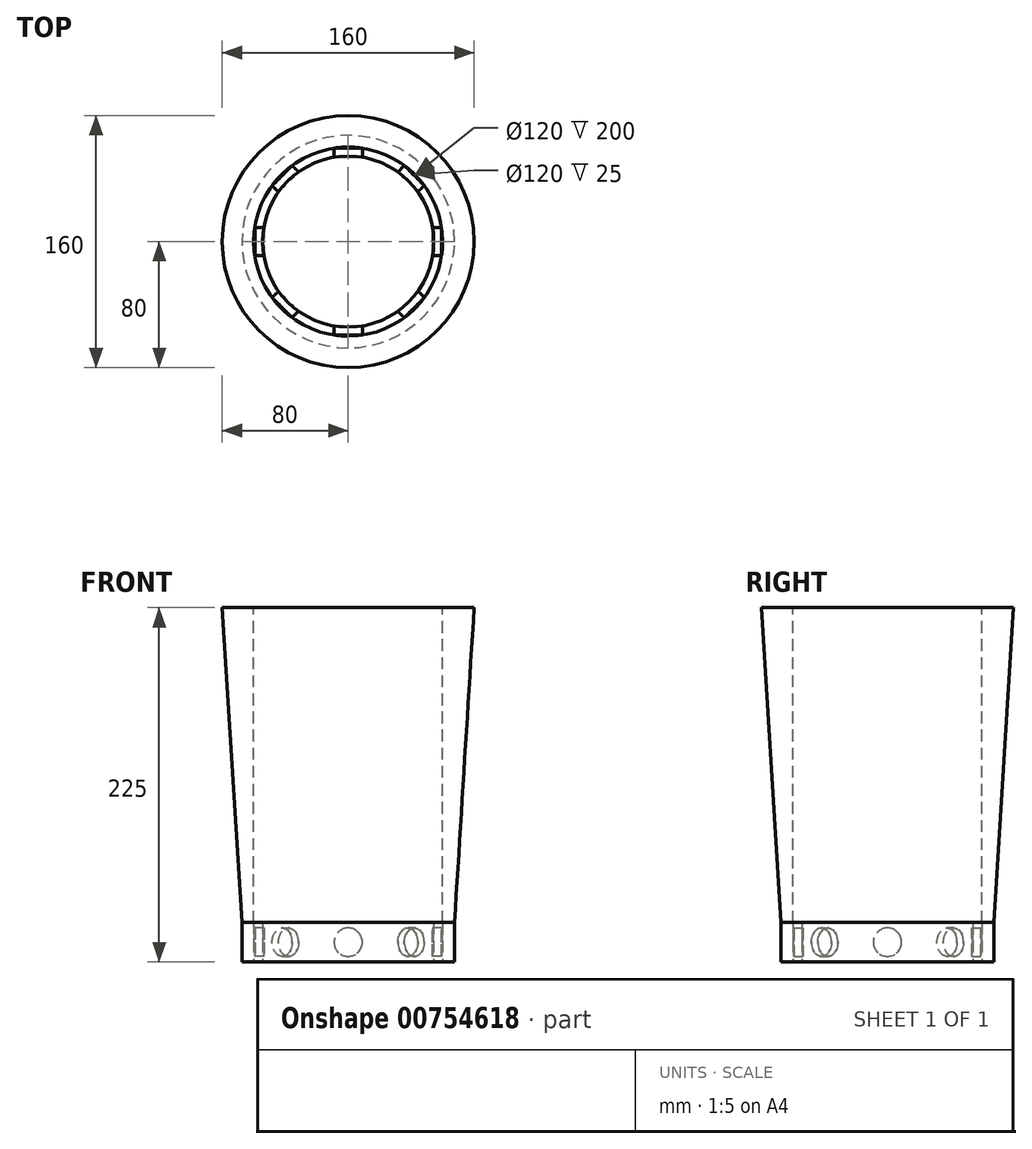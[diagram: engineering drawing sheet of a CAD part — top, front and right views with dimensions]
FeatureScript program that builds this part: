
annotation { "Feature Type Name" : "Feature", "Feature Type Description" : "" }
export const myFeature = defineFeature(function(context is Context, id is Id, definition is map)
    precondition{}
    {
        {
            var Q0;
            Q0=qCreatedBy(makeId("Top.planeOp"),FACE);
            var sketch = newSketch(context, id + "F0", { "sketchPlane" : qUnion([Q0])});
            skCircle(sketch, "E0", {"center": v(0, 0) * mm, "radius": 67.5 * mm});
            skSolve(sketch);
        }
        {
            var Q0;
            Q0=qCreatedBy(makeId("Top.planeOp"),FACE);
            cPlane(context, id + "F1", {"entities" : qUnion([Q0]), "cplaneType" : CPlaneType.OFFSET, "offset" : 200 * mm, "width" : 150 * mm, "height" : 150 * mm});
        }
        {
            var Q0;
            Q0=qCreatedBy(id+"F1.planeOp",FACE);
            var sketch = newSketch(context, id + "F2", { "sketchPlane" : qUnion([Q0])});
            skPoint(sketch, "E1", {"position": v(0, 0) * mm});
            skCircle(sketch, "E2", {"center": v(0, 0) * mm, "radius": 80 * mm});
            skSolve(sketch);
        }
        {
            var Q0;
            Q0=makeQuery(id+"F0.imprint","IMPRINT",FACE,{"disambiguationData":[TD([[makeQuery(id+"F0.imprint","IMPRINT",EDGE,{"derivedFrom":sQuery(id+"F0.wireOp",EDGE,"E0")}),1.0]])]});
            var Q1;
            Q1=makeQuery(id+"F2.imprint","IMPRINT",FACE,{"disambiguationData":[TD([[makeQuery(id+"F2.imprint","IMPRINT",EDGE,{"derivedFrom":sQuery(id+"F2.wireOp",EDGE,"E2")}),1.0]])]});
            loft(context, id + "F3", {"sheetProfilesArray" : [{ "sheetProfileEntities" : qUnion([Q0]) }, { "sheetProfileEntities" : qUnion([Q1]) }]});
        }
        {
            var Q0;
            Q0=makeQuery(id+"F3.opLoft","CAP_FACE",FACE,{"disambiguationData":[OSD([makeQuery(id+"F2.imprint","IMPRINT",FACE,{"disambiguationData":[TD([[makeQuery(id+"F2.imprint","IMPRINT",EDGE,{"derivedFrom":sQuery(id+"F2.wireOp",EDGE,"E2")}),1.0]])]})])],"isStart":true});
            var sketch = newSketch(context, id + "F4", { "sketchPlane" : qUnion([Q0])});
            skCircle(sketch, "E3", {"center": v(0, 0) * mm, "radius": 60 * mm});
            skSolve(sketch);
        }
        {
            var Q0;
            Q0=makeQuery(id+"F4.imprint","IMPRINT",FACE,{"disambiguationData":[TD([[makeQuery(id+"F4.imprint","IMPRINT",EDGE,{"derivedFrom":sQuery(id+"F4.wireOp",EDGE,"E3")}),1.0]])]});
            extrude(context, id + "F5", {"entities" : qUnion([Q0]), "operationType" : NewBodyOperationType.REMOVE, "oppositeDirection" : true, "depth" : 200 * mm, "offsetDistance" : 25 * mm});
        }
        {
            var Q0;
            Q0=qCreatedBy(makeId("Top.planeOp"),FACE);
            cPlane(context, id + "F6", {"entities" : qUnion([Q0]), "cplaneType" : CPlaneType.OFFSET, "offset" : 12.5 * mm, "oppositeDirection" : true, "width" : 150 * mm, "height" : 150 * mm});
        }
        {
            var Q0;
            Q0=qCreatedBy(id+"F6.planeOp",FACE);
            var sketch = newSketch(context, id + "F7", { "sketchPlane" : qUnion([Q0])});
            skPoint(sketch, "E4", {"position": v(0, 0) * mm});
            skCircle(sketch, "E5", {"center": v(0, 0) * mm, "radius": 67.5 * mm});
            skCircle(sketch, "E6", {"center": v(0, 0) * mm, "radius": 60 * mm});
            skLineSegment(sketch, "E7", {"start": v(-93.29, 0) * mm, "end": v(108.22, 0) * mm});
            skLineSegment(sketch, "E8", {"start": v(0, 89.91) * mm, "end": v(0, -108.53) * mm});
            skLineSegment(sketch, "E9", {"start": v(0, 0) * mm, "end": v(91.24, 91.24) * mm});
            skPoint(sketch, "E10", {"position": v(60, 0) * mm});
            skPoint(sketch, "E11", {"position": v(54.32, 0) * mm});
            skLineSegment(sketch, "E12", {"start": v(0, 0) * mm, "end": v(78.64, -78.64) * mm});
            skLineSegment(sketch, "E13", {"start": v(0, 0) * mm, "end": v(-76.82, -76.82) * mm});
            skLineSegment(sketch, "E14", {"start": v(0, 0) * mm, "end": v(-81.4, 81.4) * mm});
            skPoint(sketch, "E15", {"position": v(38.41, -38.41) * mm});
            skPoint(sketch, "E16", {"position": v(42.43, -42.43) * mm});
            skPoint(sketch, "E17", {"position": v(0, -60) * mm});
            skPoint(sketch, "E18", {"position": v(0, -54.32) * mm});
            skPoint(sketch, "E19", {"position": v(-42.43, -42.43) * mm});
            skPoint(sketch, "E20", {"position": v(-38.41, -38.41) * mm});
            skPoint(sketch, "E21", {"position": v(-60, 0) * mm});
            skPoint(sketch, "E22", {"position": v(-54.32, 0) * mm});
            skPoint(sketch, "E23", {"position": v(-42.43, 42.43) * mm});
            skPoint(sketch, "E24", {"position": v(-38.41, 38.41) * mm});
            skPoint(sketch, "E25", {"position": v(0, 60) * mm});
            skPoint(sketch, "E26", {"position": v(0, 54.32) * mm});
            skCircle(sketch, "E27", {"center": v(0, 0) * mm, "radius": 54.32 * mm});
            skPoint(sketch, "E28", {"position": v(-9, -59.32) * mm});
            skLineSegment(sketch, "E29", {"start": v(-9, -59.32) * mm, "end": v(-9, -53.57) * mm});
            skPoint(sketch, "E30", {"position": v(35.58, -48.31) * mm});
            skLineSegment(sketch, "E31", {"start": v(35.58, -48.31) * mm, "end": v(31.52, -44.24) * mm});
            skPoint(sketch, "E32", {"position": v(59.32, -9) * mm});
            skLineSegment(sketch, "E33", {"start": v(59.32, -9) * mm, "end": v(53.57, -9) * mm});
            skPoint(sketch, "E34", {"position": v(48.31, 35.58) * mm});
            skLineSegment(sketch, "E35", {"start": v(48.31, 35.58) * mm, "end": v(44.24, 31.52) * mm});
            skPoint(sketch, "E36", {"position": v(9, 59.32) * mm});
            skLineSegment(sketch, "E37", {"start": v(9, 59.32) * mm, "end": v(9, 53.57) * mm});
            skPoint(sketch, "E38", {"position": v(-35.58, 48.31) * mm});
            skLineSegment(sketch, "E39", {"start": v(-35.58, 48.31) * mm, "end": v(-31.52, 44.24) * mm});
            skPoint(sketch, "E40", {"position": v(-59.32, 9) * mm});
            skLineSegment(sketch, "E41", {"start": v(-59.32, 9) * mm, "end": v(-53.57, 9) * mm});
            skPoint(sketch, "E42", {"position": v(-48.31, -35.58) * mm});
            skLineSegment(sketch, "E43", {"start": v(-48.31, -35.58) * mm, "end": v(-44.24, -31.52) * mm});
            skSolve(sketch);
        }
        {
            var Q0;
            {var subQ0=sQuery(id+"F7.wireOp",EDGE,"E35");Q0=makeQuery(id+"F7.imprint","IMPRINT",FACE,{"disambiguationData":[TD([[makeQuery(id+"F7.imprint","IMPRINT",EDGE,{"derivedFrom":subQ0}),-1.0]])]});}
            var Q1;
            Q1=sQuery(id+"F7.wireOp",EDGE,"E9");
            revolve(context, id + "F8", {"operationType" : NewBodyOperationType.ADD, "surfaceOperationType" : NewSurfaceOperationType.NEW, "entities" : qUnion([Q0]), "axis" : qUnion([Q1]), "revolveType" : RevolveType.FULL});
        }
        {
            var Q0;
            {var subQ0=sQuery(id+"F7.wireOp",EDGE,"E29");Q0=makeQuery(id+"F7.imprint","IMPRINT",FACE,{"disambiguationData":[TD([[makeQuery(id+"F7.imprint","IMPRINT",EDGE,{"derivedFrom":subQ0}),-1.0]])]});}
            var Q1;
            {var subQ0=sQuery(id+"F7.wireOp",EDGE,"E37");Q1=makeQuery(id+"F7.imprint","IMPRINT",FACE,{"disambiguationData":[TD([[makeQuery(id+"F7.imprint","IMPRINT",EDGE,{"derivedFrom":subQ0}),-1.0]])]});}
            var Q2;
            Q2=sQuery(id+"F7.wireOp",EDGE,"E8");
            revolve(context, id + "F9", {"operationType" : NewBodyOperationType.ADD, "surfaceOperationType" : NewSurfaceOperationType.NEW, "entities" : qUnion([Q0, Q1]), "axis" : qUnion([Q2]), "revolveType" : RevolveType.FULL});
        }
        {
            var Q0;
            {var subQ0=sQuery(id+"F7.wireOp",EDGE,"E31");Q0=makeQuery(id+"F7.imprint","IMPRINT",FACE,{"disambiguationData":[TD([[makeQuery(id+"F7.imprint","IMPRINT",EDGE,{"derivedFrom":subQ0}),-1.0]])]});}
            var Q1;
            Q1=sQuery(id+"F7.wireOp",EDGE,"E12");
            revolve(context, id + "F10", {"operationType" : NewBodyOperationType.ADD, "surfaceOperationType" : NewSurfaceOperationType.NEW, "entities" : qUnion([Q0]), "axis" : qUnion([Q1]), "revolveType" : RevolveType.FULL});
        }
        {
            var Q0;
            {var subQ0=sQuery(id+"F7.wireOp",EDGE,"E39");Q0=makeQuery(id+"F7.imprint","IMPRINT",FACE,{"disambiguationData":[TD([[makeQuery(id+"F7.imprint","IMPRINT",EDGE,{"derivedFrom":subQ0}),-1.0]])]});}
            var Q1;
            Q1=sQuery(id+"F7.wireOp",EDGE,"E14");
            revolve(context, id + "F11", {"operationType" : NewBodyOperationType.ADD, "surfaceOperationType" : NewSurfaceOperationType.NEW, "entities" : qUnion([Q0]), "axis" : qUnion([Q1]), "revolveType" : RevolveType.FULL});
        }
        {
            var Q0;
            {var subQ0=sQuery(id+"F7.wireOp",EDGE,"E33");Q0=makeQuery(id+"F7.imprint","IMPRINT",FACE,{"disambiguationData":[TD([[makeQuery(id+"F7.imprint","IMPRINT",EDGE,{"derivedFrom":subQ0}),-1.0]])]});}
            var Q1;
            {var subQ0=sQuery(id+"F7.wireOp",EDGE,"E41");Q1=makeQuery(id+"F7.imprint","IMPRINT",FACE,{"disambiguationData":[TD([[makeQuery(id+"F7.imprint","IMPRINT",EDGE,{"derivedFrom":subQ0}),-1.0]])]});}
            var Q2;
            Q2=sQuery(id+"F7.wireOp",EDGE,"E7");
            revolve(context, id + "F12", {"operationType" : NewBodyOperationType.ADD, "surfaceOperationType" : NewSurfaceOperationType.NEW, "entities" : qUnion([Q0, Q1]), "axis" : qUnion([Q2]), "revolveType" : RevolveType.FULL});
        }
        {
            var Q0;
            {var subQ0=sQuery(id+"F7.wireOp",EDGE,"E43");Q0=makeQuery(id+"F7.imprint","IMPRINT",FACE,{"disambiguationData":[TD([[makeQuery(id+"F7.imprint","IMPRINT",EDGE,{"derivedFrom":subQ0}),-1.0]])]});}
            var Q1;
            Q1=sQuery(id+"F7.wireOp",EDGE,"E13");
            revolve(context, id + "F13", {"operationType" : NewBodyOperationType.ADD, "surfaceOperationType" : NewSurfaceOperationType.NEW, "entities" : qUnion([Q0]), "axis" : qUnion([Q1]), "revolveType" : RevolveType.FULL});
        }
        {
            var Q0;
            {var subQ0=sQuery(id+"F7.wireOp",EDGE,"E8");var subQ1=sQuery(id+"F7.wireOp",EDGE,"E5");var subQ2=makeQuery(id+"F7.imprint","INTERSECT",VERTEX,{"disambiguationData":[OD(1.0)],"derivedFrom":[subQ1,subQ0]});Q0=makeQuery(id+"F7.imprint","IMPRINT",FACE,{"disambiguationData":[TD([[makeQuery(id+"F7.imprint","IMPRINT",EDGE,{"disambiguationData":[TD([[subQ2,-1.0]])],"derivedFrom":subQ1}),1.0]])]});}
            var Q1;
            {var subQ4=sQuery(id+"F7.wireOp",EDGE,"E13");var subQ6=sQuery(id+"F7.wireOp",EDGE,"E5");var subQ8=makeQuery(id+"F7.imprint","INTERSECT",VERTEX,{"derivedFrom":[subQ6,subQ4]});Q1=makeQuery(id+"F7.imprint","IMPRINT",FACE,{"disambiguationData":[TD([[makeQuery(id+"F7.imprint","IMPRINT",EDGE,{"disambiguationData":[TD([[subQ8,-1.0]])],"derivedFrom":subQ6}),1.0]])]});}
            var Q2;
            {var subQ4=sQuery(id+"F7.wireOp",EDGE,"E7");var subQ6=sQuery(id+"F7.wireOp",EDGE,"E5");var subQ7=makeQuery(id+"F7.imprint","INTERSECT",VERTEX,{"disambiguationData":[OD(1.0)],"derivedFrom":[subQ6,subQ4]});Q2=makeQuery(id+"F7.imprint","IMPRINT",FACE,{"disambiguationData":[TD([[makeQuery(id+"F7.imprint","IMPRINT",EDGE,{"disambiguationData":[TD([[subQ7,-1.0]])],"derivedFrom":subQ6}),1.0]])]});}
            var Q3;
            {var subQ4=sQuery(id+"F7.wireOp",EDGE,"E5");var subQ6=sQuery(id+"F7.wireOp",EDGE,"E14");var subQ8=makeQuery(id+"F7.imprint","INTERSECT",VERTEX,{"derivedFrom":[subQ4,subQ6]});Q3=makeQuery(id+"F7.imprint","IMPRINT",FACE,{"disambiguationData":[TD([[makeQuery(id+"F7.imprint","IMPRINT",EDGE,{"disambiguationData":[TD([[subQ8,-1.0]])],"derivedFrom":subQ4}),1.0]])]});}
            var Q4;
            {var subQ0=sQuery(id+"F7.wireOp",EDGE,"E8");var subQ1=sQuery(id+"F7.wireOp",EDGE,"E5");var subQ2=makeQuery(id+"F7.imprint","INTERSECT",VERTEX,{"disambiguationData":[OD(0.0)],"derivedFrom":[subQ1,subQ0]});Q4=makeQuery(id+"F7.imprint","IMPRINT",FACE,{"disambiguationData":[TD([[makeQuery(id+"F7.imprint","IMPRINT",EDGE,{"disambiguationData":[TD([[subQ2,-1.0]])],"derivedFrom":subQ1}),1.0]])]});}
            var Q5;
            {var subQ1=sQuery(id+"F7.wireOp",EDGE,"E5");var subQ6=sQuery(id+"F7.wireOp",EDGE,"E9");var subQ8=makeQuery(id+"F7.imprint","INTERSECT",VERTEX,{"derivedFrom":[subQ1,subQ6]});Q5=makeQuery(id+"F7.imprint","IMPRINT",FACE,{"disambiguationData":[TD([[makeQuery(id+"F7.imprint","IMPRINT",EDGE,{"disambiguationData":[TD([[subQ8,-1.0]])],"derivedFrom":subQ1}),1.0]])]});}
            var Q6;
            {var subQ1=sQuery(id+"F7.wireOp",EDGE,"E5");var subQ6=sQuery(id+"F7.wireOp",EDGE,"E9");var subQ8=makeQuery(id+"F7.imprint","INTERSECT",VERTEX,{"derivedFrom":[subQ1,subQ6]});Q6=makeQuery(id+"F7.imprint","IMPRINT",FACE,{"disambiguationData":[TD([[makeQuery(id+"F7.imprint","IMPRINT",EDGE,{"disambiguationData":[TD([[subQ8,1.0]])],"derivedFrom":subQ1}),1.0]])]});}
            var Q7;
            {var subQ0=sQuery(id+"F7.wireOp",EDGE,"E7");var subQ1=sQuery(id+"F7.wireOp",EDGE,"E5");var subQ2=makeQuery(id+"F7.imprint","INTERSECT",VERTEX,{"disambiguationData":[OD(0.0)],"derivedFrom":[subQ1,subQ0]});Q7=makeQuery(id+"F7.imprint","IMPRINT",FACE,{"disambiguationData":[TD([[makeQuery(id+"F7.imprint","IMPRINT",EDGE,{"disambiguationData":[TD([[subQ2,1.0]])],"derivedFrom":subQ1}),1.0]])]});}
            extrude(context, id + "F14", {"entities" : qUnion([Q0, Q1, Q2, Q3, Q4, Q5, Q6, Q7]), "endBound" : BoundingType.SYMMETRIC, "depth" : 25 * mm, "offsetDistance" : 25 * mm});
        }
        {
            var Q0;
            {var subQ3=sQuery(id+"F7.wireOp",EDGE,"E27");var subQ6=makeQuery(id+"F7.imprint","INTERSECT",VERTEX,{"derivedFrom":[subQ3,sQuery(id+"F7.wireOp",EDGE,"E31")]});Q0=makeQuery(id+"F7.imprint","IMPRINT",FACE,{"disambiguationData":[TD([[makeQuery(id+"F7.imprint","IMPRINT",EDGE,{"disambiguationData":[TD([[subQ6,1.0]])],"derivedFrom":subQ3}),1.0]])]});}
            var Q1;
            {var subQ3=sQuery(id+"F7.wireOp",EDGE,"E27");var subQ5=makeQuery(id+"F7.imprint","INTERSECT",VERTEX,{"derivedFrom":[subQ3,sQuery(id+"F7.wireOp",EDGE,"E29")]});Q1=makeQuery(id+"F7.imprint","IMPRINT",FACE,{"disambiguationData":[TD([[makeQuery(id+"F7.imprint","IMPRINT",EDGE,{"disambiguationData":[TD([[subQ5,1.0]])],"derivedFrom":subQ3}),1.0]])]});}
            var Q2;
            {var subQ3=sQuery(id+"F7.wireOp",EDGE,"E27");var subQ5=makeQuery(id+"F7.imprint","INTERSECT",VERTEX,{"derivedFrom":[subQ3,sQuery(id+"F7.wireOp",EDGE,"E43")]});Q2=makeQuery(id+"F7.imprint","IMPRINT",FACE,{"disambiguationData":[TD([[makeQuery(id+"F7.imprint","IMPRINT",EDGE,{"disambiguationData":[TD([[subQ5,1.0]])],"derivedFrom":subQ3}),1.0]])]});}
            var Q3;
            {var subQ3=sQuery(id+"F7.wireOp",EDGE,"E27");var subQ6=makeQuery(id+"F7.imprint","INTERSECT",VERTEX,{"derivedFrom":[subQ3,sQuery(id+"F7.wireOp",EDGE,"E41")]});Q3=makeQuery(id+"F7.imprint","IMPRINT",FACE,{"disambiguationData":[TD([[makeQuery(id+"F7.imprint","IMPRINT",EDGE,{"disambiguationData":[TD([[subQ6,1.0]])],"derivedFrom":subQ3}),1.0]])]});}
            var Q4;
            {var subQ3=sQuery(id+"F7.wireOp",EDGE,"E27");var subQ5=makeQuery(id+"F7.imprint","INTERSECT",VERTEX,{"derivedFrom":[subQ3,sQuery(id+"F7.wireOp",EDGE,"E39")]});Q4=makeQuery(id+"F7.imprint","IMPRINT",FACE,{"disambiguationData":[TD([[makeQuery(id+"F7.imprint","IMPRINT",EDGE,{"disambiguationData":[TD([[subQ5,1.0]])],"derivedFrom":subQ3}),1.0]])]});}
            var Q5;
            {var subQ3=sQuery(id+"F7.wireOp",EDGE,"E27");var subQ6=makeQuery(id+"F7.imprint","INTERSECT",VERTEX,{"derivedFrom":[subQ3,sQuery(id+"F7.wireOp",EDGE,"E37")]});Q5=makeQuery(id+"F7.imprint","IMPRINT",FACE,{"disambiguationData":[TD([[makeQuery(id+"F7.imprint","IMPRINT",EDGE,{"disambiguationData":[TD([[subQ6,1.0]])],"derivedFrom":subQ3}),1.0]])]});}
            var Q6;
            {var subQ3=sQuery(id+"F7.wireOp",EDGE,"E27");var subQ6=makeQuery(id+"F7.imprint","INTERSECT",VERTEX,{"derivedFrom":[subQ3,sQuery(id+"F7.wireOp",EDGE,"E35")]});Q6=makeQuery(id+"F7.imprint","IMPRINT",FACE,{"disambiguationData":[TD([[makeQuery(id+"F7.imprint","IMPRINT",EDGE,{"disambiguationData":[TD([[subQ6,1.0]])],"derivedFrom":subQ3}),1.0]])]});}
            var Q7;
            {var subQ3=sQuery(id+"F7.wireOp",EDGE,"E27");var subQ5=makeQuery(id+"F7.imprint","INTERSECT",VERTEX,{"derivedFrom":[subQ3,sQuery(id+"F7.wireOp",EDGE,"E33")]});Q7=makeQuery(id+"F7.imprint","IMPRINT",FACE,{"disambiguationData":[TD([[makeQuery(id+"F7.imprint","IMPRINT",EDGE,{"disambiguationData":[TD([[subQ5,1.0]])],"derivedFrom":subQ3}),1.0]])]});}
            extrude(context, id + "F15", {"entities" : qUnion([Q0, Q1, Q2, Q3, Q4, Q5, Q6, Q7]), "endBound" : BoundingType.SYMMETRIC, "depth" : 25 * mm, "offsetDistance" : 25 * mm});
        }
    });
